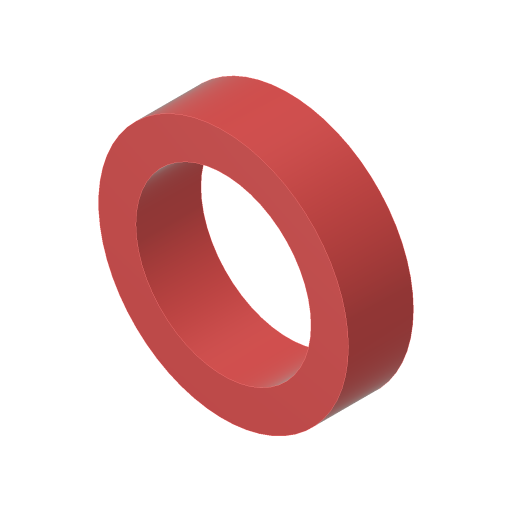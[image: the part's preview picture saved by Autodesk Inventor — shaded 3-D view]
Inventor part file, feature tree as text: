
AUTODESK INVENTOR PART (.ipt)
format: ipt  version: 2023.4 (Build 274418000, 418)  size: 112,640 bytes
history: native  units: in
note: dims shown in document units (in); Inventor stores cm internally (conversion verified against a paired STEP export)
features: extrude x1, sketch x1
ambient origin geometry x8: Origin, YZ Plane, XZ Plane, XY Plane, X Axis, Y Axis, Z Axis, Center Point
bodies: Solid1 (feature_tree)
feature tree (2):
  extrude  "Extrusion1"  Depth=0.2175in
  sketch  "Sketch1"  dims[d0=0.585in d1=0.125in d2=0.2175in d3=0.0in]
